# Revit family: Hager-VOLTA-Hollow_wall-IP30-With_Cover-With_DIN-Hosted-SE-en
name_source: partatom
category: Electrical Equipment
units: mm (PartAtom-declared; Revit-internal decimal feet)

## family parameters
Cut with Voids When Loaded = No
Host = Face
Maintain Annotation Orientation = Yes
Panel Configuration = Two Columns, Circuits Across
Part Type = Panelboard
Room Calculation Point = No
Round Connector Dimension = Use Diameter
Shared = No

## types (9) — shared parameters
BC_MODEL_ID = 1547279
BC_OBJECT_ID = 513509
BC_OBJECT_VERSION = #1
Code hager = ADD-EC000214_EU
EF000003 - Mounting method = Hollow wall
EF000008 - Width = 348 mm  [stored 1.14173 ft]
EF000024 - UV resistant = No
EF000116 - RAL-number = 9010
EF000118 - With mounting plate = No
EF001062 - EMC-version = No
EF001134 - DIN-rail = Yes
EF002950 - Width in number of modular spacings = 12
EF005474 - Degree of protection (IP) = IP30
EF006244 - Transparent cover/door = No
EF006306 - With lock = No
EF015941 - Signal passing door = No
ETIM class code = EC000214
ETIM class name = Small distribution board
HG000001-Number of columns = 1
HG000002-With door or cover = Yes
HG000003-Range = VOLTA
HG000005-Thickness = 2 mm  [stored 0.00656168 ft]
HG000006-Flush mounted = Yes
HG000009-Double swing door = No
HG000010-Asymmetric doors = No
HG000012-Door swing angle = 90.00°
HG000013-Door on the left = No
HG000014-Door on the right = Yes
HG000015-Clearance visibility = Yes
HG000016-Door 3D visibility = Yes
HG000017-Distance between poles = 18 mm  [stored 0.0590551 ft]
HG000060-RAL-number = 9010
HG000099-Onfly Template ID = 507532
HGEF002950-Width in number of modular spacings = 12
Manufacturer = Hager
Name = VOLTA-Hollow_wall-IP30-With_Cover-With_DIN-SE
Name BIM&CO = Electricity
Name hager = ADD_Enclosures_EC000214
Uniformat = Low Tension Service & Dist.
Uniformat code = D501001
zero-valued in all types: Default Elevation, EF001131 - Inner depth, HG000007-Number of empty columns

## per-type parameters (varying)
| type | BC_VARIANT_ID | EF000007 - Colour | EF000040 - Height | EF000049 - Depth | EF000218 - Built-in depth | EF000266 - Number of rows | EF000332 - Built-in height | EF000846 - Built-in width | EF001088 - Extension possible | EF004462 - Type of closure | EF009212 - Cover model | EF015776 - Earthing terminal block | EF015777 - Neutral terminal block | HG000004-Manufacturer reference | HG000008-Number of empty rows | HG000011-Empty rows from bottom | HGEF000266-Number of rows |
| VOLTA-Hollow_wall_W348_H356_D94_12_Modular_Spacing-VH12NN | 1174443 | White | 356 mm  [stored 1.16798 ft] | 94 mm  [stored 0.308399 ft] | 90 mm  [stored 0.295276 ft] | 1 | 321 mm  [stored 1.05315 ft] | 314 mm  [stored 1.03018 ft] | Yes | Other | With notch | Yes | Yes | VH12NN | 0 | No | 1 |
| VOLTA-Hollow_wall_W348_H505_D94_12_Modular_Spacing-VH24NN | 1174446 | White | 505 mm  [stored 1.65682 ft] | 94 mm  [stored 0.308399 ft] | 90 mm  [stored 0.295276 ft] | 2 | 470 mm  [stored 1.54199 ft] | 314 mm  [stored 1.03018 ft] | Yes | Other | With notch | Yes | Yes | VH24NN | 0 | No | 2 |
| VOLTA-Hollow_wall_W348_H630_D94_12_Modular_Spacing-VH36NN | 1174447 | White | 630 mm  [stored 2.06693 ft] | 94 mm  [stored 0.308399 ft] | 90 mm  [stored 0.295276 ft] | 3 | 595 mm  [stored 1.9521 ft] | 314 mm  [stored 1.03018 ft] | Yes | Other | With notch | Yes | Yes | VH36NN | 0 | No | 3 |
| VOLTA-Hollow_wall_W348_H755_D94_12_Modular_Spacing-VH48NN | 1174448 | White | 755 mm  [stored 2.47703 ft] | 94 mm  [stored 0.308399 ft] | 90 mm  [stored 0.295276 ft] | 4 | 720 mm  [stored 2.3622 ft] | 314 mm  [stored 1.03018 ft] | Yes | Other | With notch | Yes | Yes | VH48NN | 0 | No | 4 |
| VOLTA-Hollow_wall_W348_H880_D98_12_Modular_Spacing-VH602NWH | 1174449 |  | 880 mm  [stored 2.88714 ft] | 98 mm  [stored 0.321522 ft] | 89 mm  [stored 0.291995 ft] | 6 | 846 mm  [stored 2.77559 ft] | 315 mm | No |  |  | No | No | VH602NWH | 4 | Yes | 6 |
| VOLTA-Hollow_wall_W348_H880_D98_12_Modular_Spacing-VH602WWH | 1174450 |  | 880 mm  [stored 2.88714 ft] | 98 mm  [stored 0.321522 ft] | 89 mm  [stored 0.291995 ft] | 6 | 846 mm  [stored 2.77559 ft] | 315 mm | No |  |  | No | No | VH602WWH | 4 | Yes | 6 |
| VOLTA-Hollow_wall_W348_H880_D98_12_Modular_Spacing-VH603NWH | 1174451 |  | 880 mm  [stored 2.88714 ft] | 98 mm  [stored 0.321522 ft] | 89 mm  [stored 0.291995 ft] | 6 | 846 mm  [stored 2.77559 ft] | 315 mm | No |  |  | No | No | VH603NWH | 3 | Yes | 6 |
| VOLTA-Hollow_wall_W348_H880_D98_12_Modular_Spacing-VH603WWH | 1174452 |  | 880 mm  [stored 2.88714 ft] | 98 mm  [stored 0.321522 ft] | 89 mm  [stored 0.291995 ft] | 6 | 846 mm  [stored 2.77559 ft] | 315 mm | No |  |  | No | No | VH603WWH | 3 | Yes | 6 |
| VOLTA-Hollow_wall_W348_H880_D98_12_Modular_Spacing-VH60NN | 1174453 | White | 880 mm  [stored 2.88714 ft] | 98 mm  [stored 0.321522 ft] | 90 mm  [stored 0.295276 ft] | 5 | 880 mm  [stored 2.88714 ft] | 314 mm  [stored 1.03018 ft] | Yes | Other | With notch | Yes | Yes | VH60NN | 0 | No | 5 |

note: column(s) folded — value = type name in every type: Reference

note: [stored X ft] marks values corroborated as IEEE doubles in the binary element streams (Revit-internal decimal feet)

## geometry (parser evidence)
native form markers: Sweep x15
no freeform markers — native parametric forms only
